# Revit family: Shower_Head-Grohe-26409_Series
name_source: partatom
category: Plumbing Fixtures
revit_build: Autodesk Revit 2018 (Build: 20170223_1515(x64)
units: mm (PartAtom-declared; Revit-internal decimal feet)

## family parameters
Cut with Voids When Loaded = No
Host = Face
OmniClass Number = 23.45.05.14.17
OmniClass Title = Showers
Part Type = Normal
Room Calculation Point = No
Round Connector Dimension = Use Diameter
Shared = Yes

## types (2) — shared parameters
Assembly Code = D2010710
CW Connection = Yes
CWFU = 1.5
Default Elevation = 0"
Description = Shower Head 1 Spray
Flow Rate = 1.75 gpm
HW Connection = Yes
HWFU = 1.5
Height = 2 1/2"
Length = 8 1/4"
Manufacturer = Grohe
Price = Prices may vary. Please consult Manufacturer Representative for most up-to-date price list.
Product Documentation Link = https://americanstandard.box.com
Product Page URL = https://www.grohe.us
URL = https://www.grohe.us
Vent Connection = No
WFU = 2
Warranty Information = Limited Lifetime Warranty
Waste Connection = No
Water Connection diameter = 1/2"
Width = 8 1/4"

## per-type parameters (varying)
| type | Body Material | Material |
| 26409000 | Metal-Grohe-000-Starlight Chrome | Metal-Grohe-000-Starlight Chrome |
| 26409EN0 | Metal-Grohe-EN0-Brushed Nickel Infinity Finish | Metal-Grohe-EN0-Brushed Nickel Infinity Finish |

note: column(s) folded — value = type name in every type: Model

## geometry (parser evidence)
native form markers: Sweep x3
no freeform markers — native parametric forms only
